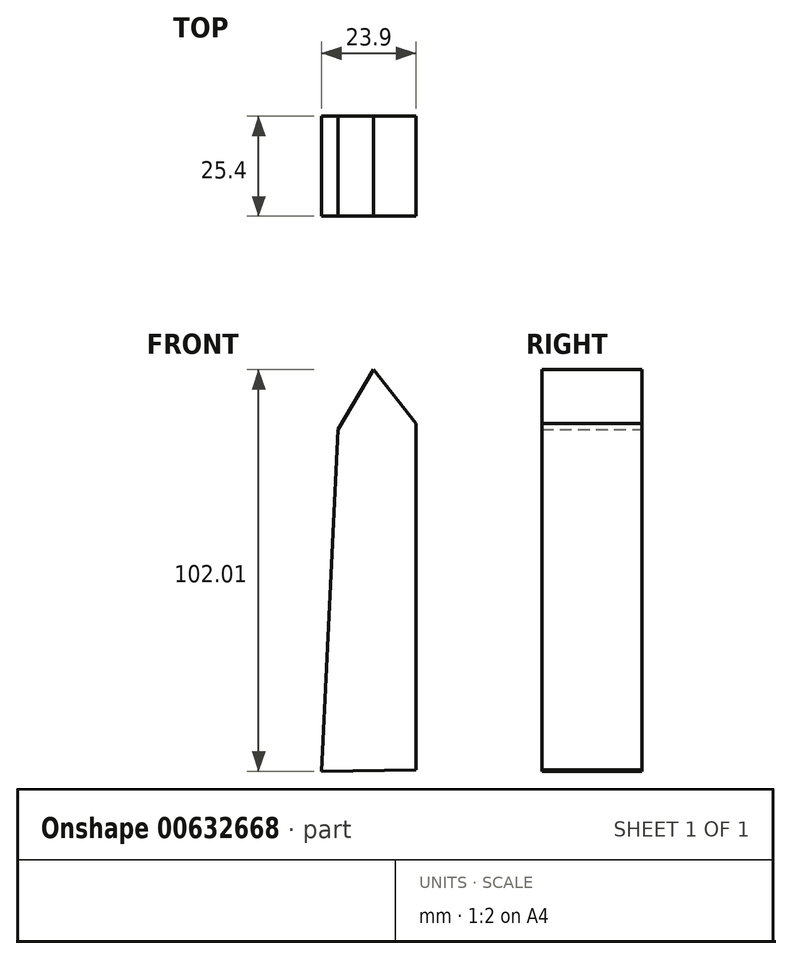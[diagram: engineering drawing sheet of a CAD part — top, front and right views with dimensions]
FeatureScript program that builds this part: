
annotation { "Feature Type Name" : "Feature", "Feature Type Description" : "" }
export const myFeature = defineFeature(function(context is Context, id is Id, definition is map)
    precondition{}
    {
        {
            var Q0;
            Q0=qCreatedBy(makeId("Front.planeOp"),FACE);
            var sketch = newSketch(context, id + "F0", { "sketchPlane" : qUnion([Q0])});
            skLineSegment(sketch, "E0", {"start": v(-67.48, -75.5) * mm, "end": v(-63.4, 11.37) * mm});
            skLineSegment(sketch, "E1", {"start": v(-63.4, 11.37) * mm, "end": v(-54.36, 26.52) * mm});
            skLineSegment(sketch, "E2", {"start": v(-54.36, 26.52) * mm, "end": v(-43.58, 12.82) * mm});
            skLineSegment(sketch, "E3", {"start": v(-43.58, 12.82) * mm, "end": v(-43.58, -71.12) * mm});
            skLineSegment(sketch, "E4", {"start": v(-43.58, -71.12) * mm, "end": v(-43.58, -75.2) * mm});
            skLineSegment(sketch, "E5", {"start": v(-43.58, -75.2) * mm, "end": v(-67.48, -75.5) * mm});
            skSolve(sketch);
        }
        {
            var Q0;
            Q0=makeQuery(id+"F0.imprint","IMPRINT",FACE,{"disambiguationData":[TD([[makeQuery(id+"F0.imprint","IMPRINT",EDGE,{"derivedFrom":sQuery(id+"F0.wireOp",EDGE,"E0")}),-1.0]])]});
            extrude(context, id + "F1", {"entities" : qUnion([Q0]), "depth" : 25.4 * mm, "offsetDistance" : 25.4 * mm});
        }
    });
